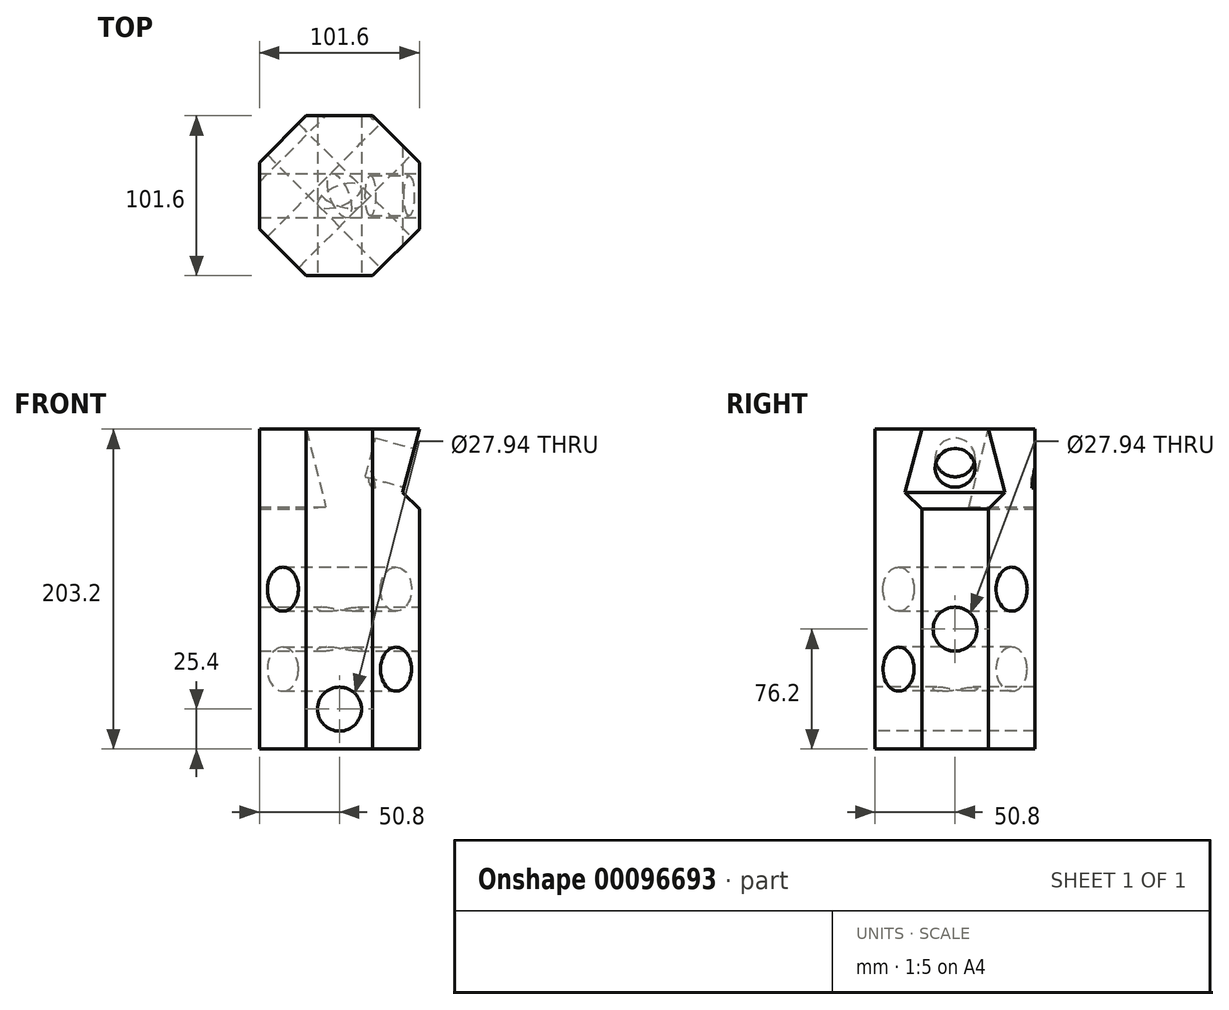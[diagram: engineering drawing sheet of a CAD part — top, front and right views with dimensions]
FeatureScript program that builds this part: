
annotation { "Feature Type Name" : "Feature", "Feature Type Description" : "" }
export const myFeature = defineFeature(function(context is Context, id is Id, definition is map)
    precondition{}
    {
        {
            var Q0;
            Q0=qCreatedBy(makeId("Top.planeOp"),FACE);
            var sketch = newSketch(context, id + "F0", { "sketchPlane" : qUnion([Q0])});
            skCircle(sketch, "E0.cCircle", {"center": v(0, 0) * mm, "radius": 50.8 * mm, "construction": true});
            skLineSegment(sketch, "E0.0", {"start": v(21.04, -50.8) * mm, "end": v(-21.04, -50.8) * mm});
            skLineSegment(sketch, "E0.1", {"start": v(-21.04, -50.8) * mm, "end": v(-50.8, -21.04) * mm});
            skLineSegment(sketch, "E0.2", {"start": v(-50.8, -21.04) * mm, "end": v(-50.8, 21.04) * mm});
            skLineSegment(sketch, "E0.3", {"start": v(-50.8, 21.04) * mm, "end": v(-21.04, 50.8) * mm});
            skLineSegment(sketch, "E0.4", {"start": v(-21.04, 50.8) * mm, "end": v(21.04, 50.8) * mm});
            skLineSegment(sketch, "E0.5", {"start": v(21.04, 50.8) * mm, "end": v(50.8, 21.04) * mm});
            skLineSegment(sketch, "E0.6", {"start": v(50.8, 21.04) * mm, "end": v(50.8, -21.04) * mm});
            skLineSegment(sketch, "E0.7", {"start": v(50.8, -21.04) * mm, "end": v(21.04, -50.8) * mm});
            skPoint(sketch, "E0.0.midPoint", {"position": v(0, -50.8) * mm});
            skSolve(sketch);
        }
        {
            var Q0;
            Q0=makeQuery(id+"F0.imprint","IMPRINT",FACE,{"disambiguationData":[TD([[makeQuery(id+"F0.imprint","IMPRINT",EDGE,{"derivedFrom":sQuery(id+"F0.wireOp",EDGE,"E0.0")}),-1.0]])]});
            extrude(context, id + "F1", {"entities" : qUnion([Q0]), "depth" : 203.2 * mm});
        }
        {
            var Q0;
            Q0=makeQuery(id+"F1.opExtrude","SWEPT_FACE",FACE,{"disambiguationData":[OSD([sQuery(id+"F0.wireOp",EDGE,"E0.0")])]});
            var sketch = newSketch(context, id + "F2", { "sketchPlane" : qUnion([Q0])});
            skCircle(sketch, "E1", {"center": v(0, 25.4) * mm, "radius": 13.97 * mm});
            skSolve(sketch);
        }
        {
            var Q0;
            Q0 = qSketchRegion(id + "F2", true);
            extrude(context, id + "F3", {"entities" : qUnion([Q0]), "operationType" : NewBodyOperationType.REMOVE, "endBound" : BoundingType.THROUGH_ALL, "oppositeDirection" : true, "depth" : 25.4 * mm});
        }
        {
            var Q0;
            Q0=makeQuery(id+"F1.opExtrude","SWEPT_FACE",FACE,{"disambiguationData":[OSD([sQuery(id+"F0.wireOp",EDGE,"E0.7")])]});
            var sketch = newSketch(context, id + "F4", { "sketchPlane" : qUnion([Q0])});
            skCircle(sketch, "E2", {"center": v(0, 50.8) * mm, "radius": 13.97 * mm});
            skPoint(sketch, "E2.centerSnap0", {"position": v(0, 0) * mm});
            skSolve(sketch);
        }
        {
            var Q0;
            Q0=makeQuery(id+"F4.imprint","IMPRINT",FACE,{"disambiguationData":[TD([[makeQuery(id+"F4.imprint","IMPRINT",EDGE,{"derivedFrom":sQuery(id+"F4.wireOp",EDGE,"E2")}),1.0]])]});
            extrude(context, id + "F5", {"entities" : qUnion([Q0]), "operationType" : NewBodyOperationType.REMOVE, "oppositeDirection" : true, "depth" : 101.6 * mm});
        }
        {
            var Q0;
            Q0=makeQuery(id+"F1.opExtrude","SWEPT_FACE",FACE,{"disambiguationData":[OSD([sQuery(id+"F0.wireOp",EDGE,"E0.6")])]});
            var sketch = newSketch(context, id + "F6", { "sketchPlane" : qUnion([Q0])});
            skCircle(sketch, "E3", {"center": v(0, 76.2) * mm, "radius": 13.97 * mm});
            skPoint(sketch, "E3.centerSnap0", {"position": v(0, 0) * mm});
            skSolve(sketch);
        }
        {
            var Q0;
            Q0 = qSketchRegion(id + "F6", true);
            extrude(context, id + "F7", {"entities" : qUnion([Q0]), "operationType" : NewBodyOperationType.REMOVE, "endBound" : BoundingType.THROUGH_ALL, "oppositeDirection" : true, "depth" : 25.4 * mm});
        }
        {
            var Q0;
            Q0=makeQuery(id+"F1.opExtrude","SWEPT_FACE",FACE,{"disambiguationData":[OSD([sQuery(id+"F0.wireOp",EDGE,"E0.5")])]});
            var sketch = newSketch(context, id + "F8", { "sketchPlane" : qUnion([Q0])});
            skCircle(sketch, "E4", {"center": v(0, 101.6) * mm, "radius": 13.97 * mm});
            skSolve(sketch);
        }
        {
            var Q0;
            Q0 = qSketchRegion(id + "F8", true);
            extrude(context, id + "F9", {"entities" : qUnion([Q0]), "operationType" : NewBodyOperationType.REMOVE, "endBound" : BoundingType.THROUGH_ALL, "oppositeDirection" : true, "depth" : 25.4 * mm});
        }
        {
            var Q0;
            Q0=makeQuery(id+"F1.opExtrude","SWEPT_FACE",FACE,{"disambiguationData":[OSD([sQuery(id+"F0.wireOp",EDGE,"E0.0")])]});
            var sketch = newSketch(context, id + "F10", { "sketchPlane" : qUnion([Q0])});
            skLineSegment(sketch, "E5", {"start": v(50.8, 203.2) * mm, "end": v(40.06, 163.14) * mm});
            skLineSegment(sketch, "E6", {"start": v(40.06, 163.14) * mm, "end": v(50.8, 152.4) * mm});
            skLineSegment(sketch, "E7", {"start": v(50.8, 152.4) * mm, "end": v(50.8, 203.2) * mm});
            skSolve(sketch);
        }
        {
            var Q0;
            Q0 = qSketchRegion(id + "F10", true);
            extrude(context, id + "F11", {"entities" : qUnion([Q0]), "operationType" : NewBodyOperationType.REMOVE, "endBound" : BoundingType.THROUGH_ALL, "oppositeDirection" : true, "depth" : 25.4 * mm});
        }
        {
            var Q0;
            Q0=makeQuery(id+"F11.boolean.opBoolean","COPY",FACE,{"derivedFrom":makeQuery(id+"F11.opExtrude","SWEPT_FACE",FACE,{"disambiguationData":[OSD([sQuery(id+"F10.wireOp",EDGE,"E5")])]})});
            var sketch = newSketch(context, id + "F12", { "sketchPlane" : qUnion([Q0])});
            skCircle(sketch, "E8", {"center": v(0, 184.02) * mm, "radius": 12.7 * mm});
            skPoint(sketch, "E8.centerSnap0", {"position": v(0, 209.42) * mm});
            skSolve(sketch);
        }
        {
            var Q0;
            Q0=makeQuery(id+"F12.imprint","IMPRINT",FACE,{"disambiguationData":[TD([[makeQuery(id+"F12.imprint","IMPRINT",EDGE,{"derivedFrom":sQuery(id+"F12.wireOp",EDGE,"E8")}),1.0]])]});
            extrude(context, id + "F13", {"entities" : qUnion([Q0]), "operationType" : NewBodyOperationType.REMOVE, "oppositeDirection" : true, "depth" : 25.4 * mm});
        }
        {
            var Q0;
            Q0=makeQuery(id+"F1.opExtrude","SWEPT_FACE",FACE,{"disambiguationData":[OSD([sQuery(id+"F0.wireOp",EDGE,"E0.5")])]});
            var sketch = newSketch(context, id + "F14", { "sketchPlane" : qUnion([Q0])});
            skLineSegment(sketch, "E9", {"start": v(50.8, 203.2) * mm, "end": v(42.11, 153.93) * mm});
            skLineSegment(sketch, "E10", {"start": v(42.11, 153.93) * mm, "end": v(50.8, 152.4) * mm});
            skLineSegment(sketch, "E11", {"start": v(50.8, 152.4) * mm, "end": v(50.8, 203.2) * mm});
            skSolve(sketch);
        }
        {
            var Q0;
            Q0 = qSketchRegion(id + "F14", true);
            extrude(context, id + "F15", {"entities" : qUnion([Q0]), "operationType" : NewBodyOperationType.REMOVE, "endBound" : BoundingType.THROUGH_ALL, "oppositeDirection" : true, "depth" : 25.4 * mm});
        }
        {
            var Q0;
            Q0=makeQuery(id+"F15.boolean.opBoolean","COPY",FACE,{"derivedFrom":makeQuery(id+"F15.opExtrude","SWEPT_FACE",FACE,{"disambiguationData":[OSD([sQuery(id+"F14.wireOp",EDGE,"E9")])]})});
            var sketch = newSketch(context, id + "F16", { "sketchPlane" : qUnion([Q0])});
            skPoint(sketch, "E12.centerSnap0", {"position": v(-35.75, 205.85) * mm});
            skLineSegment(sketch, "E13", {"start": v(-35.75, 205.85) * mm, "end": v(-22.66, 130.52) * mm, "construction": true});
            skCircle(sketch, "E14", {"center": v(-31.4, 180.83) * mm, "radius": 12.7 * mm});
            skSolve(sketch);
        }
        {
            var Q0;
            Q0 = qSketchRegion(id + "F16", true);
            extrude(context, id + "F17", {"entities" : qUnion([Q0]), "operationType" : NewBodyOperationType.REMOVE, "oppositeDirection" : true, "depth" : 25.4 * mm});
        }
    });
